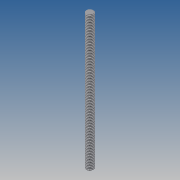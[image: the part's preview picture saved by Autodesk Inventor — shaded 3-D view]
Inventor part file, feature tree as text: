
AUTODESK INVENTOR PART (.ipt)
format: ipt  version: 2013 (Build 170138000, 138)  size: 713,216 bytes
history: native  units: mm
features: sketch x2, extrude x1, helix x1, projected_geometry x1
ambient origin geometry x8: Origin, YZ Plane, XZ Plane, XY Plane, X Axis, Y Axis, Z Axis, Center Point
bodies: Solid1 (feature_tree)
feature tree (5):
  extrude  "Extrusion1"  Depth=150.0mm TaperAngle=0.0deg
  helix  "Coil1"  [1 undecoded]
  sketch  "Sketch1"  dims[d0=8.0mm d2=150.0mm d3=0.0mm d4=5.061455mm]
  sketch  "Sketch2"  dims[d5=0.8mm d7=0.75mm d8=1.5mm d9=200.0mm d10=10.0mm d11=0.0mm d12=90.0deg d13=90.0deg d14=0.0mm d15=0.0mm]
  projected_geometry  "Project Cut Edges1"
note: 1 required parameter value undecoded (feature->parameter linkage not recoverable at this tier; creation-order binding heuristic only, values carry confidence <= 0.55)
